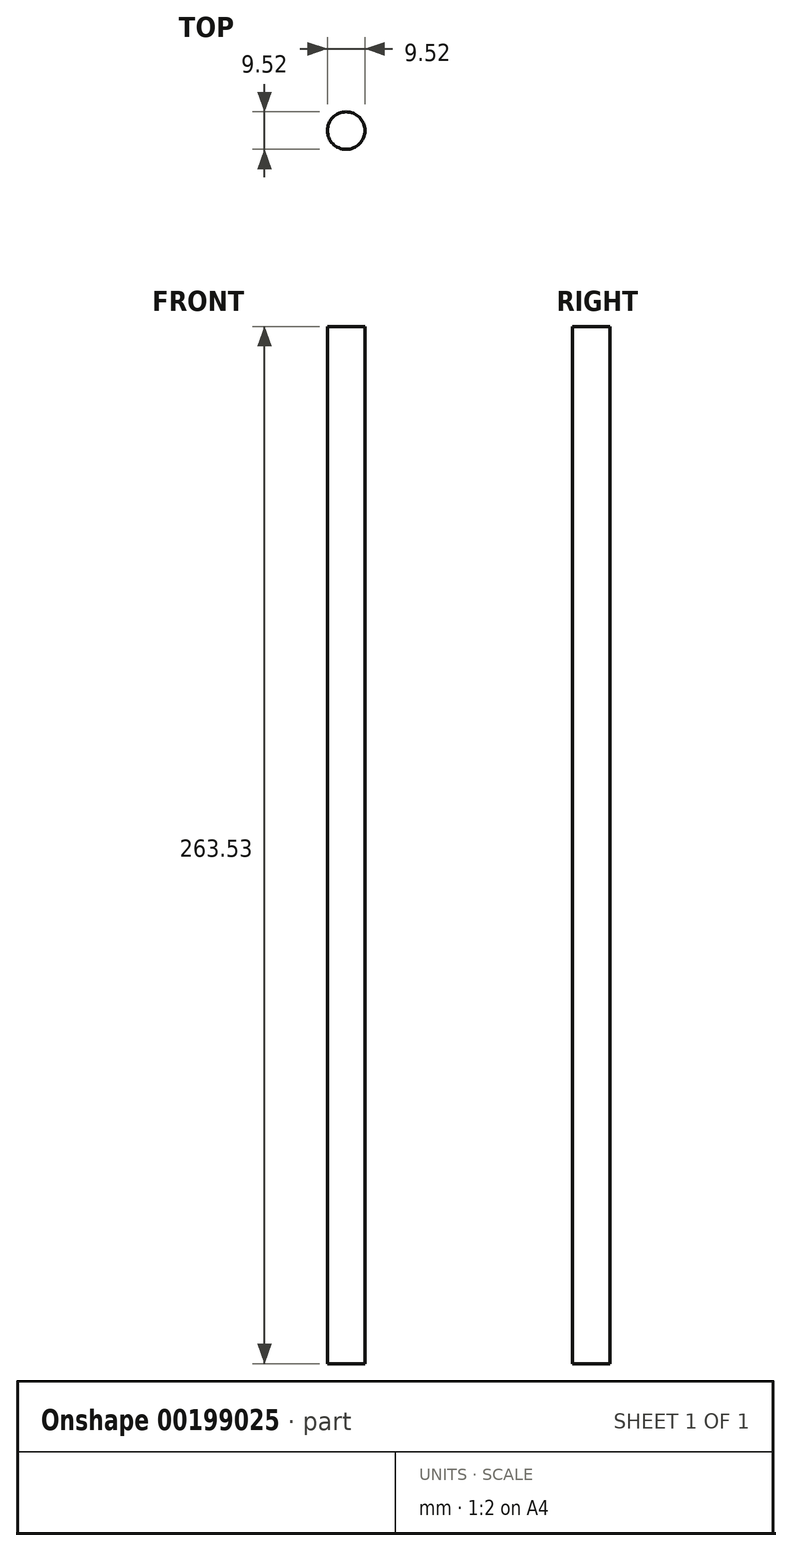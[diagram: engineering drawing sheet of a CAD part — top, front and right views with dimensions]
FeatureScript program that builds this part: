
annotation { "Feature Type Name" : "Feature", "Feature Type Description" : "" }
export const myFeature = defineFeature(function(context is Context, id is Id, definition is map)
    precondition{}
    {
        {
            var Q0;
            Q0=qCreatedBy(makeId("Top.planeOp"),FACE);
            var sketch = newSketch(context, id + "F0", { "sketchPlane" : qUnion([Q0])});
            skCircle(sketch, "E0", {"center": v(0, 0) * mm, "radius": 4.76 * mm});
            skSolve(sketch);
        }
        {
            var Q0;
            Q0 = qSketchRegion(id + "F0", true);
            extrude(context, id + "F1", {"entities" : qUnion([Q0]), "depth" : 263.52 * mm});
        }
    });
